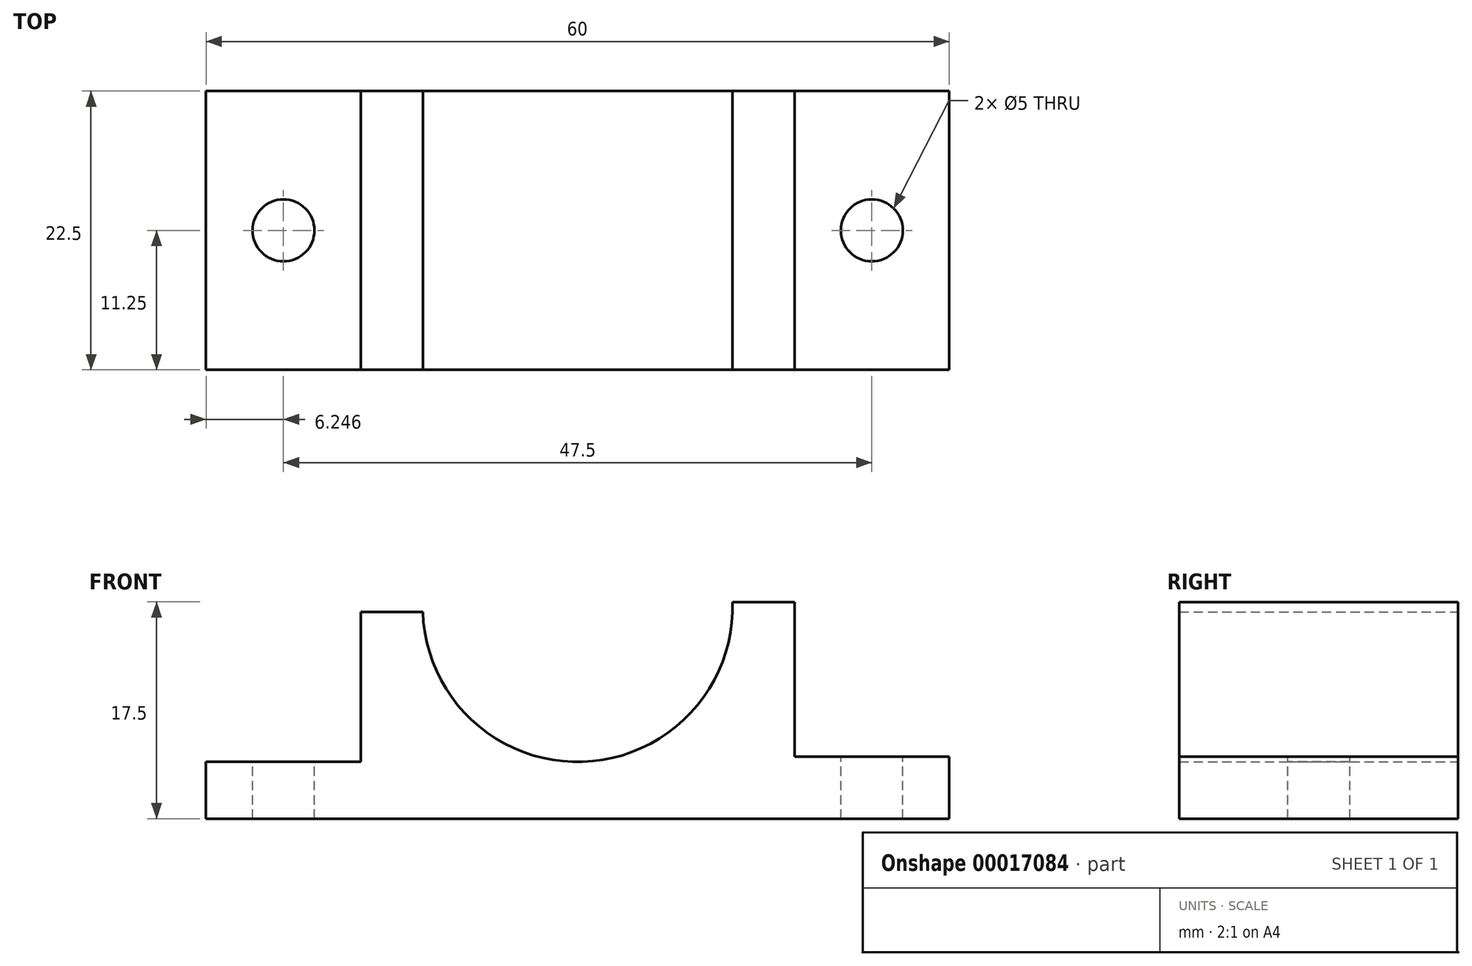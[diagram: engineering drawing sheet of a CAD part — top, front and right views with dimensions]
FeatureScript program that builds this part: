
annotation { "Feature Type Name" : "Feature", "Feature Type Description" : "" }
export const myFeature = defineFeature(function(context is Context, id is Id, definition is map)
    precondition{}
    {
        {
            var Q0;
            Q0=qCreatedBy(makeId("Front.planeOp"),FACE);
            var sketch = newSketch(context, id + "F0", { "sketchPlane" : qUnion([Q0])});
            skLineSegment(sketch, "E0", {"start": v(-45.28, -15.8) * mm, "end": v(14.72, -15.8) * mm});
            skLineSegment(sketch, "E1", {"start": v(14.72, -15.8) * mm, "end": v(14.72, -10.8) * mm});
            skLineSegment(sketch, "E2", {"start": v(14.72, -10.8) * mm, "end": v(2.22, -10.8) * mm});
            skLineSegment(sketch, "E3", {"start": v(2.22, -10.8) * mm, "end": v(2.22, 1.7) * mm});
            skLineSegment(sketch, "E4", {"start": v(-45.28, -15.8) * mm, "end": v(-45.28, -11.2) * mm});
            skLineSegment(sketch, "E5", {"start": v(-45.28, -11.2) * mm, "end": v(-32.78, -11.2) * mm});
            skLineSegment(sketch, "E6", {"start": v(-32.78, -11.2) * mm, "end": v(-32.78, 0.88) * mm});
            skLineSegment(sketch, "E7", {"start": v(-32.78, 0.88) * mm, "end": v(-27.78, 0.88) * mm});
            skLineSegment(sketch, "E8", {"start": v(2.22, 1.7) * mm, "end": v(-2.78, 1.7) * mm});
            skArc(sketch, "E9", {"start": v(-27.78, 0.88) * mm, "mid": v(-14.88, -11.21) * mm, "end": v(-2.78, 1.7) * mm});
            skSolve(sketch);
        }
        {
            var Q0;
            Q0=makeQuery(id+"F0.imprint","IMPRINT",FACE,{"disambiguationData":[TD([[makeQuery(id+"F0.imprint","IMPRINT",EDGE,{"derivedFrom":sQuery(id+"F0.wireOp",EDGE,"E0")}),1.0]])]});
            extrude(context, id + "F1", {"entities" : qUnion([Q0]), "depth" : 22.5 * mm});
        }
        {
            var Q0;
            Q0=makeQuery(id+"F1.opExtrude","SWEPT_FACE",FACE,{"disambiguationData":[OSD([sQuery(id+"F0.wireOp",EDGE,"E5")])]});
            var sketch = newSketch(context, id + "F2", { "sketchPlane" : qUnion([Q0])});
            skCircle(sketch, "E10", {"center": v(-39.03, -11.25) * mm, "radius": 2.5 * mm});
            skSolve(sketch);
        }
        {
            var Q0;
            Q0=makeQuery(id+"F2.imprint","IMPRINT",FACE,{"disambiguationData":[TD([[makeQuery(id+"F2.imprint","IMPRINT",EDGE,{"derivedFrom":sQuery(id+"F2.wireOp",EDGE,"E10")}),1.0]])]});
            extrude(context, id + "F3", {"entities" : qUnion([Q0]), "operationType" : NewBodyOperationType.REMOVE, "oppositeDirection" : true, "depth" : 25 * mm});
        }
        {
            var Q0;
            Q0=makeQuery(id+"F1.opExtrude","SWEPT_FACE",FACE,{"disambiguationData":[OSD([sQuery(id+"F0.wireOp",EDGE,"E2")])]});
            var sketch = newSketch(context, id + "F4", { "sketchPlane" : qUnion([Q0])});
            skCircle(sketch, "E11", {"center": v(8.47, -11.25) * mm, "radius": 2.5 * mm});
            skSolve(sketch);
        }
        {
            var Q0;
            Q0 = qSketchRegion(id + "F4", true);
            extrude(context, id + "F5", {"entities" : qUnion([Q0]), "operationType" : NewBodyOperationType.REMOVE, "endBound" : BoundingType.THROUGH_ALL, "oppositeDirection" : true, "depth" : 25 * mm});
        }
    });
